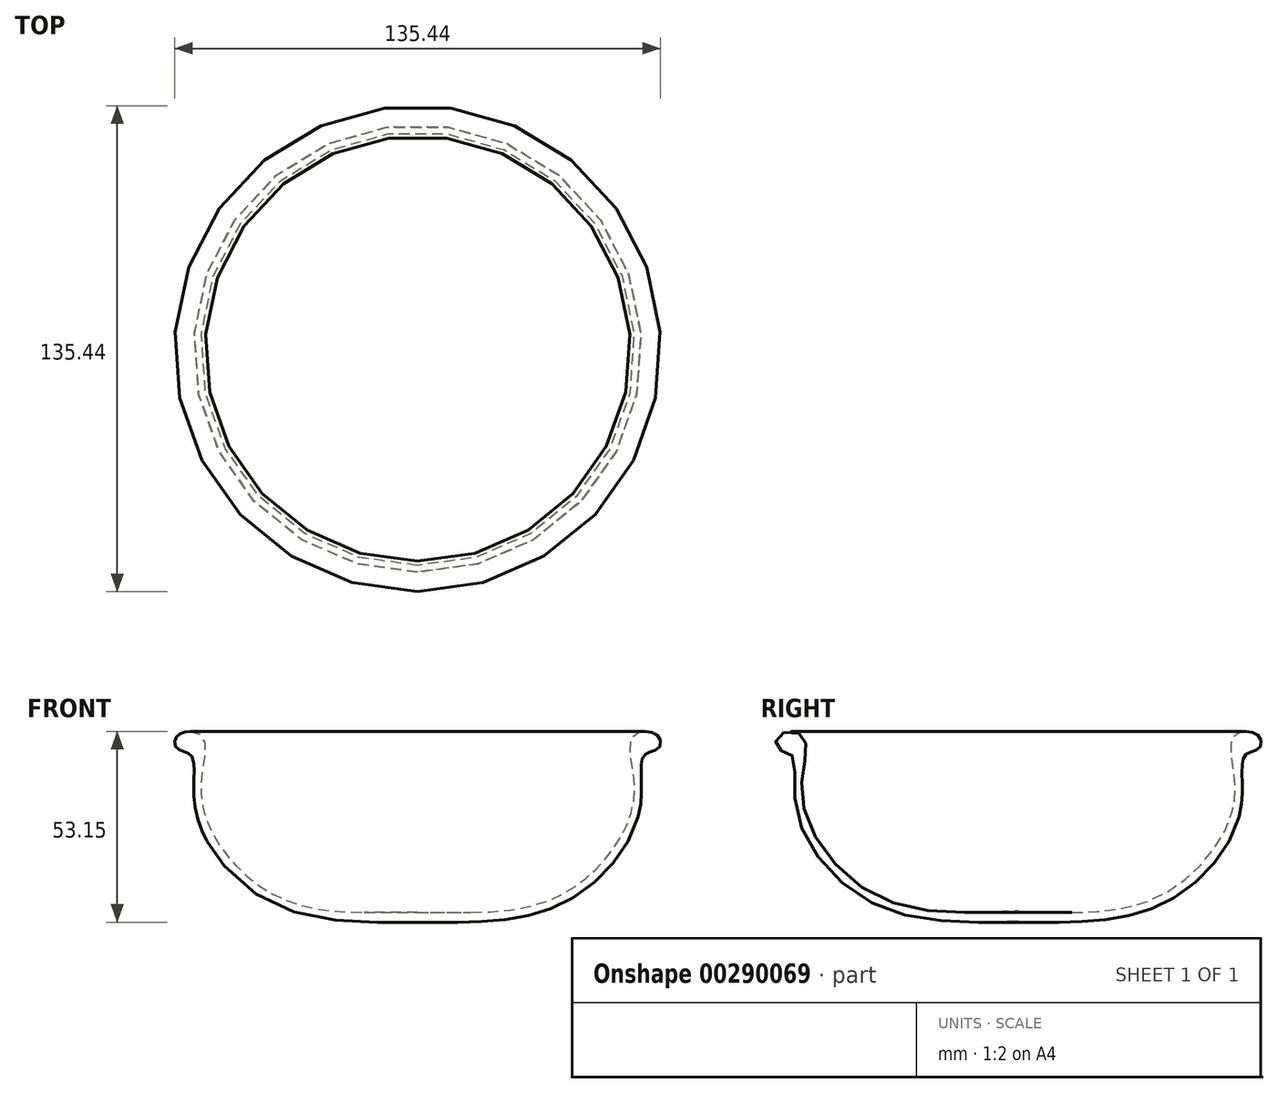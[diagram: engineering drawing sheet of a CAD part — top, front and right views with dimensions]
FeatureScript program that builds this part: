
annotation { "Feature Type Name" : "Feature", "Feature Type Description" : "" }
export const myFeature = defineFeature(function(context is Context, id is Id, definition is map)
    precondition{}
    {
        {
            var Q0;
            Q0=qCreatedBy(makeId("Right.planeOp"),FACE);
            var sketch = newSketch(context, id + "F0", { "sketchPlane" : qUnion([Q0])});
            skFitSpline(sketch, "E0", {"points": [v(0, 0) * mm, v(-40.34, 4.96) * mm, v(-61.84, 30.73) * mm, v(-63.14, 46.3) * mm, v(-67.03, 48.16) * mm, v(-67.03, 51.68) * mm, v(-61.1, 52.42) * mm, v(-59.25, 47.6) * mm, v(-59.99, 32.22) * mm, v(-39.96, 7.37) * mm, v(0, 3.1) * mm], "startDerivative": vector(-272.86, -8.23) * mm, "endDerivative": vector(274.41, 16.1) * mm});
            skLineSegment(sketch, "E1", {"start": v(0, 3.1) * mm, "end": v(0, 0) * mm});
            skSolve(sketch);
        }
        {
            var Q0;
            Q0 = qSketchRegion(id + "F0", true);
            var Q1;
            Q1=sQuery(id+"F0.wireOp",EDGE,"E1");
            revolve(context, id + "F1", {"entities" : qUnion([Q0]), "axis" : qUnion([Q1]), "revolveType" : RevolveType.FULL});
        }
    });
